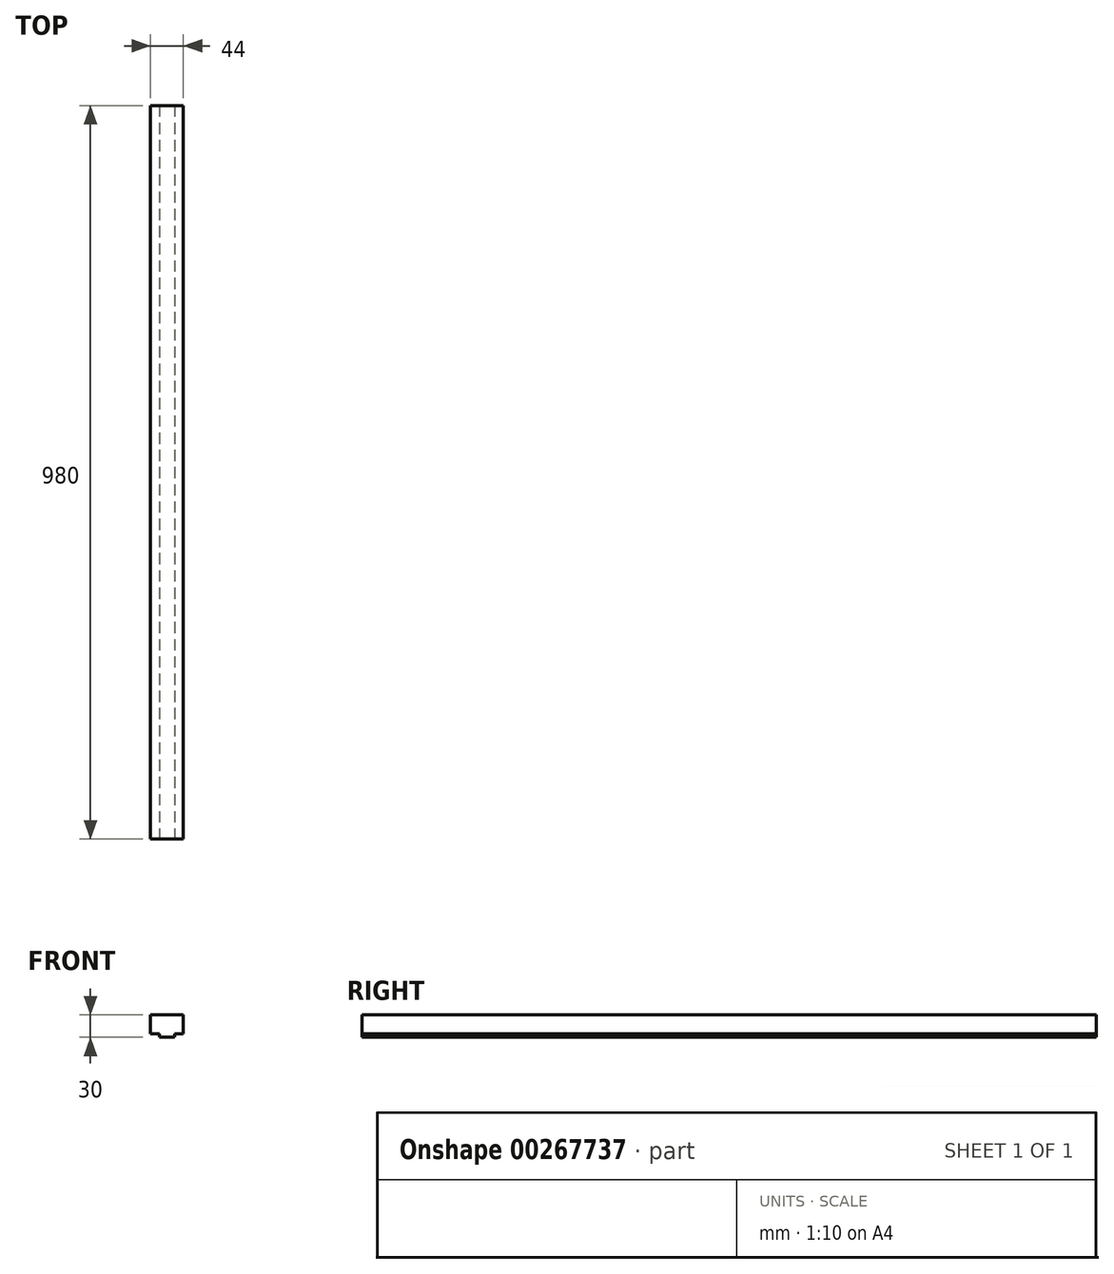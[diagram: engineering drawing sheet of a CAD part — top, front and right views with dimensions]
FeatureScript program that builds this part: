
annotation { "Feature Type Name" : "Feature", "Feature Type Description" : "" }
export const myFeature = defineFeature(function(context is Context, id is Id, definition is map)
    precondition{}
    {
        {
            var Q0;
            Q0=qCreatedBy(makeId("Front.planeOp"),FACE);
            var sketch = newSketch(context, id + "F0", { "sketchPlane" : qUnion([Q0])});
            skLineSegment(sketch, "E0.bottom", {"start": v(10, -15) * mm, "end": v(-10, -15) * mm});
            skLineSegment(sketch, "E0.top", {"start": v(22, 15) * mm, "end": v(-22, 15) * mm});
            skLineSegment(sketch, "E0.left", {"start": v(22, -10.4) * mm, "end": v(22, 15) * mm});
            skLineSegment(sketch, "E0.right", {"start": v(-22, -10.4) * mm, "end": v(-22, 15) * mm});
            skPoint(sketch, "E0.middle", {"position": v(0, 0) * mm});
            skLineSegment(sketch, "E1", {"start": v(0, -23.3) * mm, "end": v(-10, -23.3) * mm, "construction": true});
            skLineSegment(sketch, "E2", {"start": v(-10, -23.3) * mm, "end": v(-10, 2.5) * mm, "construction": true});
            skLineSegment(sketch, "E3", {"start": v(-10, 2.5) * mm, "end": v(10, 2.5) * mm, "construction": true});
            skLineSegment(sketch, "E4", {"start": v(10, 2.5) * mm, "end": v(10, -15) * mm, "construction": true});
            skLineSegment(sketch, "E5", {"start": v(-10, -15) * mm, "end": v(-10, -10.4) * mm});
            skLineSegment(sketch, "E6", {"start": v(-10, -10.4) * mm, "end": v(-22, -10.4) * mm});
            skLineSegment(sketch, "E7", {"start": v(10, -10.4) * mm, "end": v(22, -10.4) * mm});
            skLineSegment(sketch, "E8", {"start": v(10, -10.4) * mm, "end": v(10, -15) * mm});
            skPoint(sketch, "E9", {"position": v(0, 15) * mm});
            skSolve(sketch);
        }
        {
            var Q0;
            Q0=qSketchRegion(id+"F0",true);
            extrude(context, id + "F1", {"entities" : qUnion([Q0]), "oppositeDirection" : true, "depth" : 980 * mm});
        }
    });
